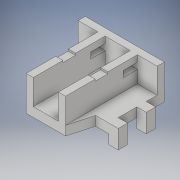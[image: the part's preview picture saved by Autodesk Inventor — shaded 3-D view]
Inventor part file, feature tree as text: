
AUTODESK INVENTOR PART (.ipt)
format: ipt  version: 2018 (Build 220112000, 112)  size: 201,728 bytes
history: native  units: in
note: dims shown in document units (in); Inventor stores cm internally (conversion verified against a paired STEP export)
features: extrude x6, sketch x6, other x3
ambient origin geometry x8: Origin, YZ Plane, XZ Plane, XY Plane, X Axis, Y Axis, Z Axis, Center Point
bodies: Solid1 (feature_tree)
feature tree (15):
  other  "Talon.ipt"
  extrude  "Extrusion1"  TaperAngle=0.0deg  [1 undecoded]
  extrude  "Extrusion4"  Depth=0.2in TaperAngle=0.0deg
  extrude  "Extrusion5"  TaperAngle=0.0deg  [1 undecoded]
  extrude  "Extrusion6"  TaperAngle=0.0deg  [1 undecoded]
  extrude  "Extrusion7"  TaperAngle=0.0deg  [1 undecoded]
  extrude  "Extrusion8"  Depth=0.13in TaperAngle=0.0deg
  other  "Solid1::Talon.ipt"
  other  "TaggingFeature1"
  sketch  "Sketch1"  dims[d0=0.3937in d1=0.0in]
  sketch  "Sketch4"  dims[d2=0.0in d3=0.2in d4=0.0in]
  sketch  "Sketch5"  dims[d10=0.26in d11=0.0in]
  sketch  "Sketch6"  dims[d12=0.5in d13=0.0in d14=0.0in]
  sketch  "Sketch7"  dims[d15=0.13in d16=0.0in]
  sketch  "Sketch8"  dims[d17=0.13in d18=0.0in d19=0.13in d20=0.0in d23=0.26in d24=0.13in d25=0.13in d26=0.0in d27=0.13in d28=0.0in]
note: 4 required parameter values undecoded (feature->parameter linkage not recoverable at this tier; creation-order binding heuristic only, values carry confidence <= 0.55)
